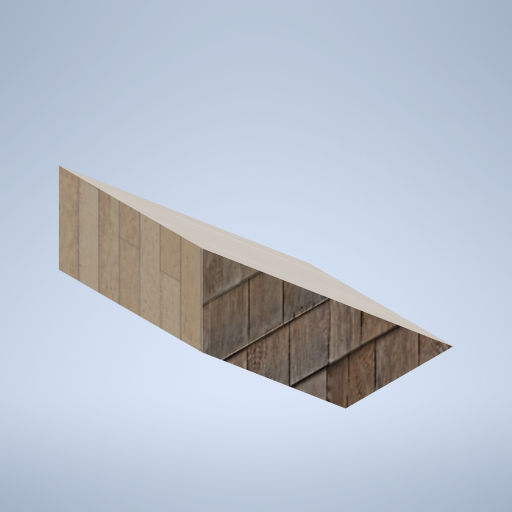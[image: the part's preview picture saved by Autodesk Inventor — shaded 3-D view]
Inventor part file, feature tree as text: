
AUTODESK INVENTOR PART (.ipt)
format: ipt  version: 2024.2 (Build 282272000, 272)  size: 332,288 bytes
history: native  units: mm
features: extrude x1, sketch x1
ambient origin geometry x8: Origin, YZ Plane, XZ Plane, XY Plane, X Axis, Y Axis, Z Axis, Center Point
bodies: Body1 (feature_tree)
feature tree (2):
  extrude  "Extrusion3"  Depth=400.0mm
  sketch  "Sketch1"  dims[d2=300.0mm d11=8.726646mm d12=8.726646mm d13=400.0mm d14=0.0mm]
